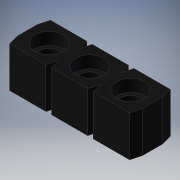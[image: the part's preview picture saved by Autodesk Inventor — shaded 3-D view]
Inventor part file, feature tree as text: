
AUTODESK INVENTOR PART (.ipt)
format: ipt  version: 2019 (Build 230136000, 136)  size: 183,808 bytes
history: native  units: in
note: dims shown in document units (in); Inventor stores cm internally (conversion verified against a paired STEP export)
features: other x49, sketch x4, extrude x3, pattern_linear x3, hole x1
ambient origin geometry x8: Origin, YZ Plane, XZ Plane, XY Plane, X Axis, Y Axis, Z Axis, Center Point
bodies: Solid1 (feature_tree)
feature tree (60):
  extrude  "Extrusion1"  Depth=0.1in TaperAngle=0.0deg
  extrude  "Extrusion2"  Depth=0.1in TaperAngle=0.0deg
  pattern_linear  "Rectangular Pattern1"  Count1=3 Spacing1=0.1in
  hole  "Hole1"  [1 undecoded]
  pattern_linear  "Rectangular Pattern2"  [2 undecoded]
  extrude  "Extrusion3"  [1 undecoded]
  pattern_linear  "Rectangular Pattern3"  [2 undecoded]
  other  "socket_XY"
  other  "socket_YZ"
  other  "socket_ZX"
  other  "socket_X"
  other  "socket_Y"
  other  "socket_Z"
  other  "socket_Center"
  other  "to_pin_1_XY"
  other  "to_pin_1_YZ"
  other  "to_pin_1_ZX"
  other  "to_pin_1_X"
  other  "to_pin_1_Y"
  other  "to_pin_1_Z"
  other  "to_pin_1_Center"
  other  "to_pin_2_XY"
  other  "to_pin_2_YZ"
  other  "to_pin_2_ZX"
  other  "to_pin_2_X"
  other  "to_pin_2_Y"
  other  "to_pin_2_Z"
  other  "to_pin_2_Center"
  other  "to_pin_3_XY"
  other  "to_pin_3_YZ"
  other  "to_pin_3_ZX"
  other  "to_pin_3_X"
  other  "to_pin_3_Y"
  other  "to_pin_3_Z"
  other  "to_pin_3_Center"
  other  "to_pin2_1_XY"
  other  "to_pin2_1_YZ"
  other  "to_pin2_1_ZX"
  other  "to_pin2_1_X"
  other  "to_pin2_1_Y"
  other  "to_pin2_1_Z"
  other  "to_pin2_1_Center"
  other  "to_pin2_2_XY"
  other  "to_pin2_2_YZ"
  other  "to_pin2_2_ZX"
  other  "to_pin2_2_X"
  other  "to_pin2_2_Y"
  other  "to_pin2_2_Z"
  other  "to_pin2_2_Center"
  other  "to_pin2_3_XY"
  other  "to_pin2_3_YZ"
  other  "to_pin2_3_ZX"
  other  "to_pin2_3_X"
  other  "to_pin2_3_Y"
  other  "to_pin2_3_Z"
  other  "to_pin2_3_Center"
  sketch  "Sketch_17"  dims[d23=0.03in d24=0.0in d25=1.1811in d27=0.1in d28=0.3937in d30=0.0in d31=0.0in]
  sketch  "Sketch_3"  dims[d0=0.1in d1=0.0in d2=0.1in d3=0.0in]
  sketch  "Sketch3"  dims[d4=1.1811in d6=0.1027in d7=0.3937in d9=0.0in]
  sketch  "Sketch_7"  dims[d10=0.052in d11=0.75in d12=0.375in d13=0.25in d14=0.5635in d15=0.1in d16=0.0in d17=1.1811in d19=0.1in d20=0.3937in d22=0.0in]
note: 6 required parameter values undecoded (feature->parameter linkage not recoverable at this tier; creation-order binding heuristic only, values carry confidence <= 0.55)
